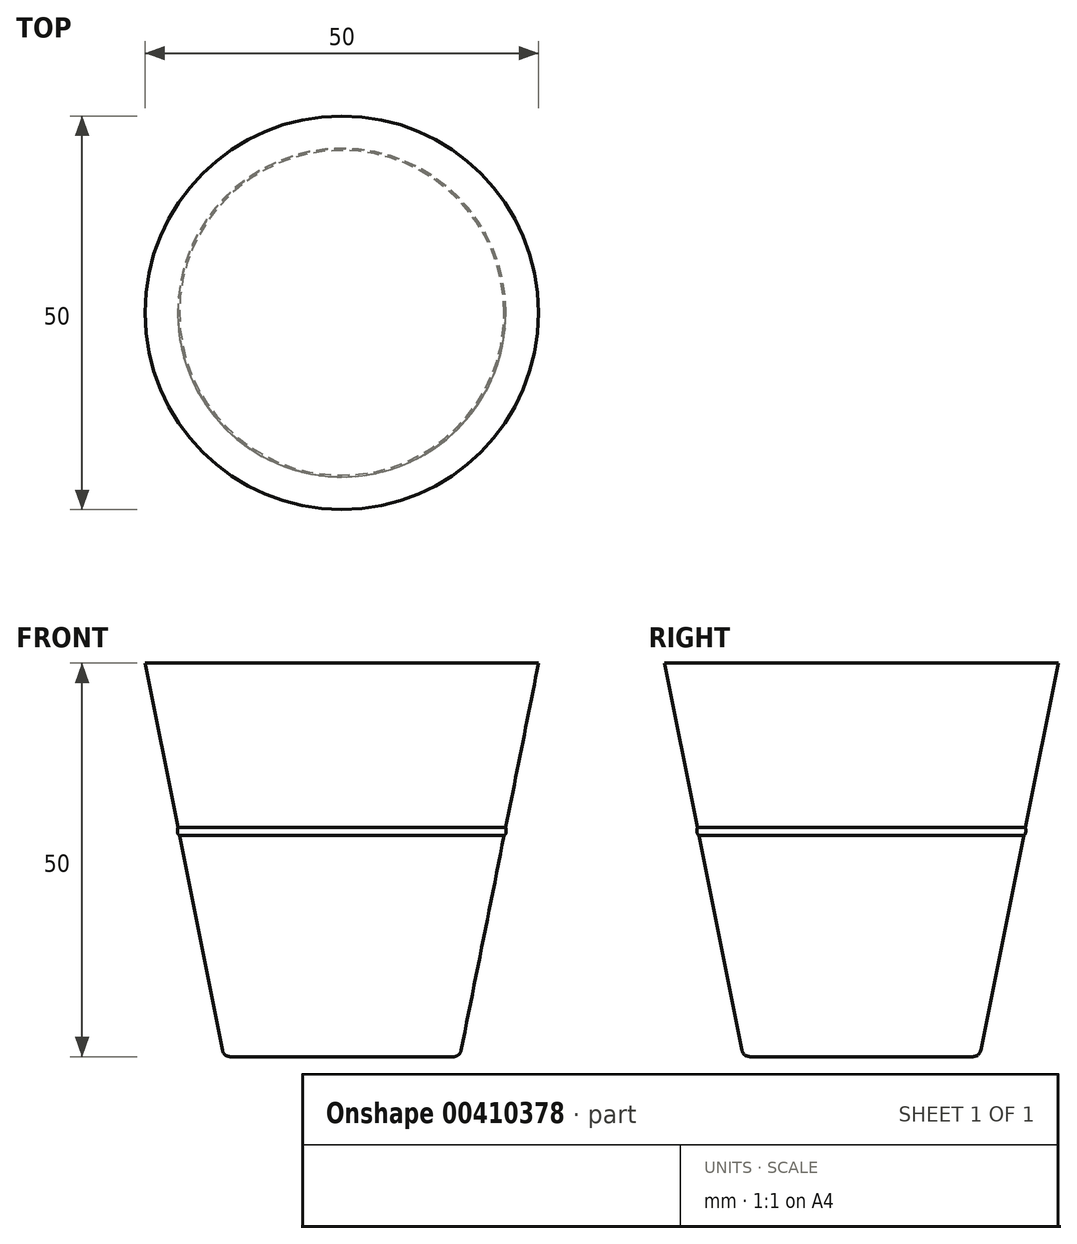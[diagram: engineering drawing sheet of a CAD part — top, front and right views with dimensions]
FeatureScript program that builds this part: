
annotation { "Feature Type Name" : "Feature", "Feature Type Description" : "" }
export const myFeature = defineFeature(function(context is Context, id is Id, definition is map)
    precondition{}
    {
        {
            var Q0;
            Q0=qCreatedBy(makeId("Front.planeOp"),FACE);
            var sketch = newSketch(context, id + "F0", { "sketchPlane" : qUnion([Q0])});
            skLineSegment(sketch, "E0", {"start": v(0, 0) * mm, "end": v(15, 0) * mm});
            skLineSegment(sketch, "E1", {"start": v(15, 0) * mm, "end": v(25, 50) * mm});
            skLineSegment(sketch, "E2", {"start": v(25, 50) * mm, "end": v(0, 50) * mm});
            skLineSegment(sketch, "E3", {"start": v(0, 50) * mm, "end": v(0, 0) * mm});
            skLineSegment(sketch, "E4", {"start": v(20.62, 28.1) * mm, "end": v(20.87, 28.1) * mm});
            skLineSegment(sketch, "E5", {"start": v(20.87, 28.1) * mm, "end": v(20.87, 29.1) * mm});
            skLineSegment(sketch, "E6", {"start": v(20.87, 29.1) * mm, "end": v(20.82, 29.1) * mm});
            skSolve(sketch);
        }
        {
            var Q0;
            Q0 = qSketchRegion(id + "F0", true);
            var Q1;
            Q1=sQuery(id+"F0.wireOp",EDGE,"E3");
            revolve(context, id + "F1", {"entities" : qUnion([Q0]), "axis" : qUnion([Q1]), "revolveType" : RevolveType.FULL});
        }
        {
            var Q0;
            Q0=makeQuery(id+"F1.opRevolve","SWEPT_EDGE",EDGE,{"disambiguationData":[OSD([sQuery(id+"F0.wireOp",EDGE,"E0"),sQuery(id+"F0.wireOp",EDGE,"E1")])]});
            fillet(context, id + "F2", {"entities" : qUnion([Q0]), "radius" : 1 * mm, "tangentPropagation" : true, "allowEdgeOverflow" : false});
        }
        {
            var Q0;
            Q0=makeQuery(id+"F1.opRevolve","SWEPT_EDGE",EDGE,{"disambiguationData":[OSD([sQuery(id+"F0.wireOp",EDGE,"E4"),sQuery(id+"F0.wireOp",EDGE,"E5")])]});
            var Q1;
            Q1=makeQuery(id+"F1.opRevolve","SWEPT_EDGE",EDGE,{"disambiguationData":[OSD([sQuery(id+"F0.wireOp",EDGE,"E5"),sQuery(id+"F0.wireOp",EDGE,"E6")])]});
            fillet(context, id + "F3", {"entities" : qUnion([Q0, Q1]), "radius" : 0.5 * mm, "tangentPropagation" : true, "allowEdgeOverflow" : false});
        }
    });
